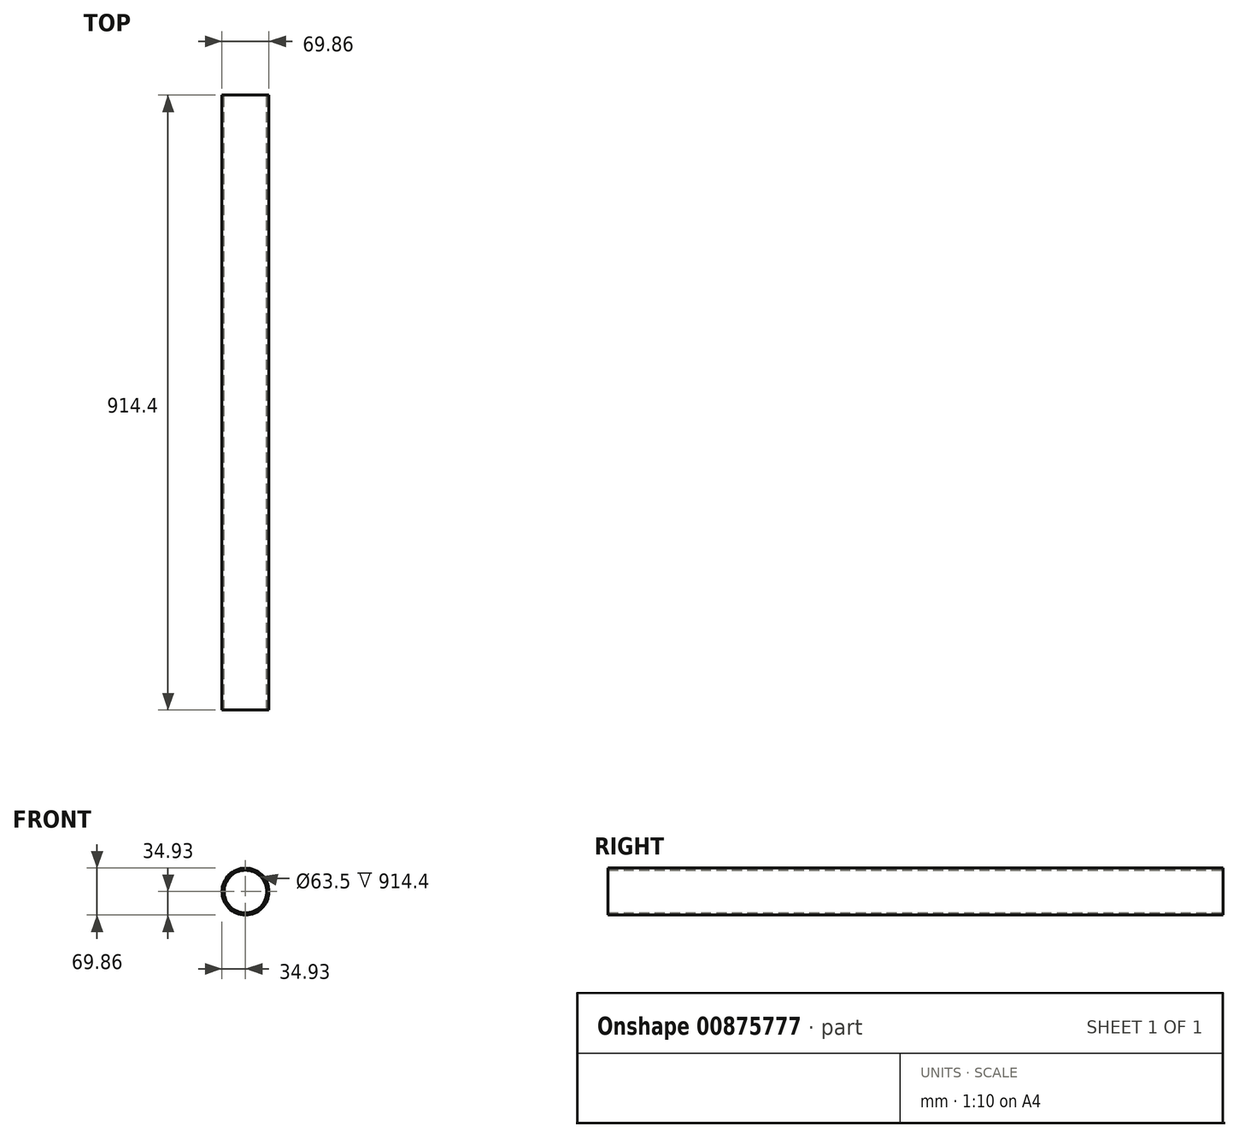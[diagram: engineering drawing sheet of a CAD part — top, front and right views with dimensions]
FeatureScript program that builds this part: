
annotation { "Feature Type Name" : "Feature", "Feature Type Description" : "" }
export const myFeature = defineFeature(function(context is Context, id is Id, definition is map)
    precondition{}
    {
        {
            var Q0;
            Q0=qCreatedBy(makeId("Front.planeOp"),FACE);
            var sketch = newSketch(context, id + "F0", { "sketchPlane" : qUnion([Q0])});
            skCircle(sketch, "E0", {"center": v(0, 0) * mm, "radius": 31.75 * mm});
            skCircle(sketch, "E1", {"center": v(0, 0) * mm, "radius": 34.93 * mm});
            skSolve(sketch);
        }
        {
            var Q0;
            Q0 = qSketchRegion(id + "F0", true);
            extrude(context, id + "F1", {"entities" : qUnion([Q0]), "depth" : 914.4 * mm, "offsetDistance" : 25.4 * mm});
        }
    });
